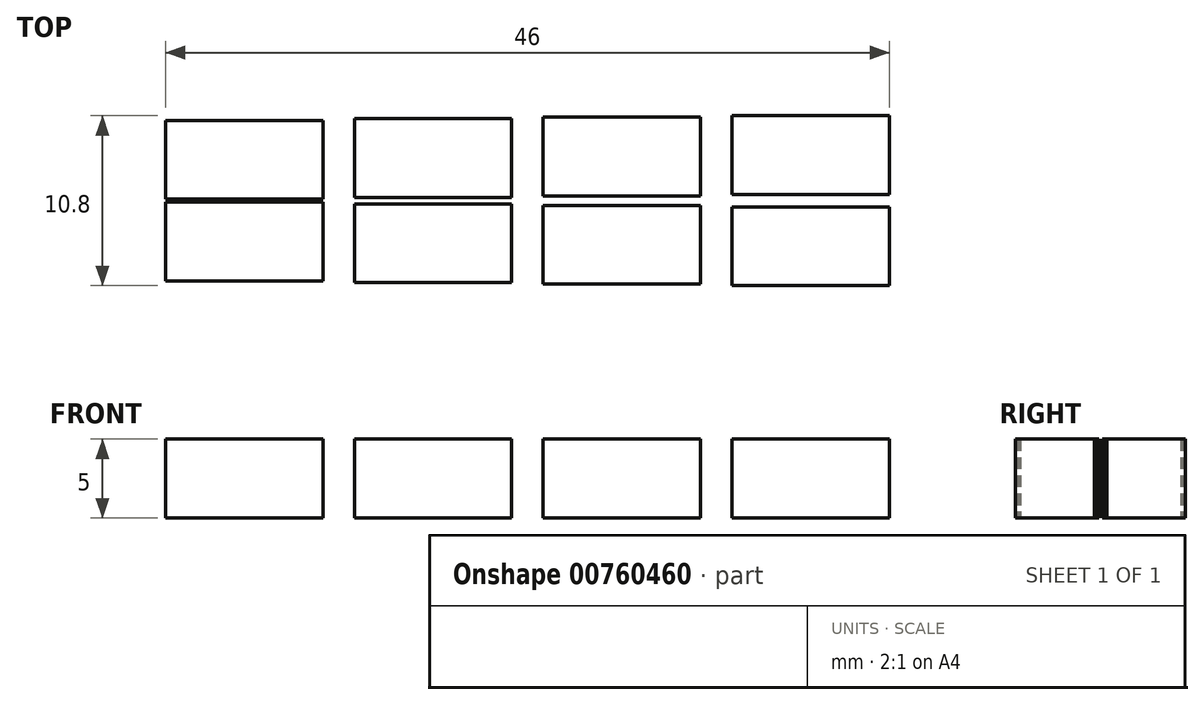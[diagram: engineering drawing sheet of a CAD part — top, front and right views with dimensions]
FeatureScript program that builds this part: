
annotation { "Feature Type Name" : "Feature", "Feature Type Description" : "" }
export const myFeature = defineFeature(function(context is Context, id is Id, definition is map)
    precondition{}
    {
        {
            var Q0;
            Q0=qCreatedBy(makeId("Top.planeOp"),FACE);
            var sketch = newSketch(context, id + "F0", { "sketchPlane" : qUnion([Q0])});
            skLineSegment(sketch, "E0", {"start": v(0, 0) * mm, "end": v(50, 0) * mm, "construction": true});
            skLineSegment(sketch, "E1.bottom", {"start": v(0, -0.1) * mm, "end": v(10, -0.1) * mm});
            skLineSegment(sketch, "E1.top", {"start": v(0, -5.1) * mm, "end": v(10, -5.1) * mm});
            skLineSegment(sketch, "E1.left", {"start": v(0, -0.1) * mm, "end": v(0, -5.1) * mm});
            skLineSegment(sketch, "E1.right", {"start": v(10, -0.1) * mm, "end": v(10, -5.1) * mm});
            skLineSegment(sketch, "E2.bottom", {"start": v(12, -0.2) * mm, "end": v(22, -0.2) * mm});
            skLineSegment(sketch, "E2.top", {"start": v(12, -5.2) * mm, "end": v(22, -5.2) * mm});
            skLineSegment(sketch, "E2.left", {"start": v(12, -0.2) * mm, "end": v(12, -5.2) * mm});
            skLineSegment(sketch, "E2.right", {"start": v(22, -0.2) * mm, "end": v(22, -5.2) * mm});
            skLineSegment(sketch, "E3.bottom", {"start": v(24, -0.3) * mm, "end": v(34, -0.3) * mm});
            skLineSegment(sketch, "E3.top", {"start": v(24, -5.3) * mm, "end": v(34, -5.3) * mm});
            skLineSegment(sketch, "E3.left", {"start": v(24, -0.3) * mm, "end": v(24, -5.3) * mm});
            skLineSegment(sketch, "E3.right", {"start": v(34, -0.3) * mm, "end": v(34, -5.3) * mm});
            skLineSegment(sketch, "E4.bottom", {"start": v(36, -0.4) * mm, "end": v(46, -0.4) * mm});
            skLineSegment(sketch, "E4.top", {"start": v(36, -5.4) * mm, "end": v(46, -5.4) * mm});
            skLineSegment(sketch, "E4.left", {"start": v(36, -0.4) * mm, "end": v(36, -5.4) * mm});
            skLineSegment(sketch, "E4.right", {"start": v(46, -0.4) * mm, "end": v(46, -5.4) * mm});
            skLineSegment(sketch, "E5.MirrorCS", {"start": v(12, 0.2) * mm, "end": v(22, 0.2) * mm});
            skLineSegment(sketch, "E6.MirrorCS", {"start": v(24, 0.3) * mm, "end": v(24, 5.3) * mm});
            skLineSegment(sketch, "E7.MirrorCS", {"start": v(22, 0.2) * mm, "end": v(22, 5.2) * mm});
            skLineSegment(sketch, "E8.MirrorCS", {"start": v(24, 5.3) * mm, "end": v(34, 5.3) * mm});
            skLineSegment(sketch, "E9.MirrorCS", {"start": v(36, 5.4) * mm, "end": v(46, 5.4) * mm});
            skLineSegment(sketch, "E10.MirrorCS", {"start": v(36, 0.4) * mm, "end": v(36, 5.4) * mm});
            skLineSegment(sketch, "E11.MirrorCS", {"start": v(24, 0.3) * mm, "end": v(34, 0.3) * mm});
            skLineSegment(sketch, "E12.MirrorCS", {"start": v(46, 0.4) * mm, "end": v(46, 5.4) * mm});
            skLineSegment(sketch, "E13.MirrorCS", {"start": v(36, 0.4) * mm, "end": v(46, 0.4) * mm});
            skLineSegment(sketch, "E14.MirrorCS", {"start": v(34, 0.3) * mm, "end": v(34, 5.3) * mm});
            skLineSegment(sketch, "E15.MirrorCS", {"start": v(12, 5.2) * mm, "end": v(22, 5.2) * mm});
            skLineSegment(sketch, "E16.MirrorCS", {"start": v(12, 0.2) * mm, "end": v(12, 5.2) * mm});
            skLineSegment(sketch, "E17.MirrorCS", {"start": v(0, 5.1) * mm, "end": v(10, 5.1) * mm});
            skLineSegment(sketch, "E18.MirrorCS", {"start": v(0, 0.1) * mm, "end": v(0, 5.1) * mm});
            skLineSegment(sketch, "E19.MirrorCS", {"start": v(0, 0.1) * mm, "end": v(10, 0.1) * mm});
            skLineSegment(sketch, "E20.MirrorCS", {"start": v(10, 0.1) * mm, "end": v(10, 5.1) * mm});
            skSolve(sketch);
        }
        {
            var Q0;
            Q0 = qSketchRegion(id + "F0", true);
            extrude(context, id + "F1", {"entities" : qUnion([Q0]), "depth" : 5 * mm, "offsetDistance" : 25 * mm});
        }
    });
